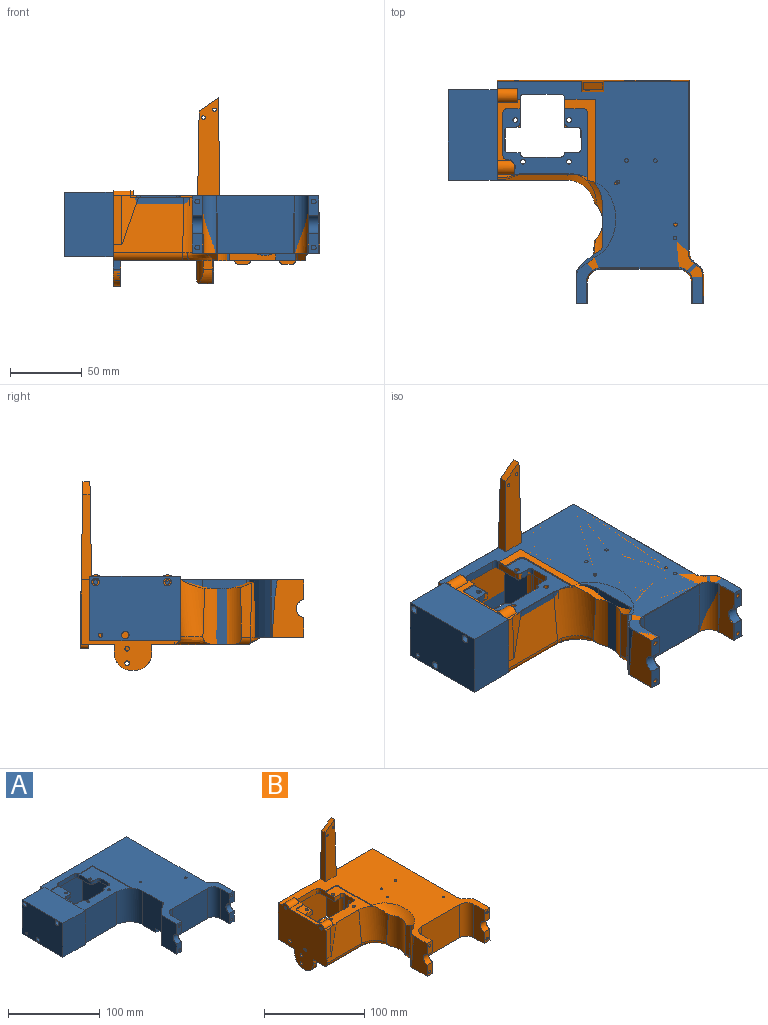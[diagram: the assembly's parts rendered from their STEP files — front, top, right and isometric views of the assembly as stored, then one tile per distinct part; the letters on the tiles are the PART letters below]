
ASSEMBLY  parts=2 mates=1
PART A: 103 faces, bbox 177.1x155.1x65.5 mm
  f0: plane 5.5x4.25mm, normal (-1,0,0), area 19.6mm2, adj f30,f55,f56,f98
  f1: plane 64.7x63mm, normal (-1,0,0), area 807.4mm2, adj f3,f24,f30,f31,f51,f84,f85,f86
  f2: plane 5.5x3.25mm, normal (-1,0,0), area 14.6mm2, adj f56,f96
  f3: plane 133.09x105mm, normal (0,0,-1), area 1435.4mm2, adj f1,f26,f33,f48,f51,f59,f61,f62
  f4: plane 17x6mm, normal (1,0,0), area 85.5mm2, adj f23,f29,f30,f55,f56,f64
  f5: plane 5x5mm, normal (0,-1,0), area 25mm2, adj f22,f23,f56,f64
  f6: plane 8x5mm, normal (0,1,0), area 40mm2, adj f20,f21,f56,f64
  f7: plane 25x5mm, normal (0,1,0), area 125mm2, adj f19,f20,f56,f64
  f8: plane 8.5x5mm, normal (0,1,0), area 42.5mm2, adj f18,f19,f56,f64
  f9: plane 12x5mm, normal (-1,0,0), area 60mm2, adj f17,f18,f56,f64
  f10: plane 5.5x5mm, normal (0,-1,0), area 27.5mm2, adj f16,f17,f56,f64
  f11: plane 17x6mm, normal (-1,0,0), area 85.5mm2, adj f16,f28,f30,f56,f57,f64
  f12: cylinder r=1.65mm len=5mm, axis (0,0,1), area 51.8mm2, adj f56,f64
  f13: cylinder r=1.65mm len=5mm, axis (0,0,1), area 51.8mm2, adj f56,f64
  f14: cylinder r=1.65mm len=5mm, axis (0,0,1), area 51.8mm2, adj f56,f64
  f15: cylinder r=1.65mm len=5mm, axis (0,0,1), area 51.8mm2, adj f56,f64
  f16: cylinder r=3mm len=5mm, axis (0,0,1), area 23.6mm2, adj f10,f11,f56,f64
  f17: cylinder r=3mm len=5mm, axis (0,0,-1), area 23.6mm2, adj f9,f10,f56,f64
  f18: cylinder r=3mm len=5mm, axis (0,0,-1), area 23.6mm2, adj f8,f9,f56,f64
  f19: cylinder r=3mm len=5mm, axis (0,0,1), area 23.6mm2, adj f7,f8,f56,f64
  f20: cylinder r=3mm len=5mm, axis (0,0,-1), area 23.6mm2, adj f6,f7,f56,f64
  f21: cylinder r=3mm len=5mm, axis (0,0,-1), area 23.6mm2, adj f6,f33,f56,f64
  f22: cylinder r=3mm len=5mm, axis (0,0,-1), area 23.6mm2, adj f5,f33,f56,f64
  f23: cylinder r=3mm len=5mm, axis (0,0,1), area 23.6mm2, adj f4,f5,f56,f64
  f24: plane 81.09x62mm, normal (0,0,-1), area 916.9mm2, adj f1,f31,f32,f33,f49,f52,f59,f60
  f25: plane 88x50.06mm, normal (0,0,-1), area 1735.8mm2, adj f26,f34,f35,f36,f37,f39,f40,f41
  f26: plane 5x5mm, normal (0,-1,0), area 25mm2, adj f3,f25,f48,f67
  f27: plane 25x6mm, normal (0,-1,0), area 150mm2, adj f28,f29,f30,f64
  f28: cylinder r=3mm len=6mm, axis (0,0,-1), area 28.3mm2, adj f11,f27,f30,f64
  f29: cylinder r=3mm len=6mm, axis (0,0,1), area 28.3mm2, adj f4,f27,f30,f64
  f30: plane 155.06x143.09mm, normal (0,0,1), area 9490.1mm2, adj f0,f1,f4,f11,f27,f28,f29,f32
  f31: plane 53.09x44mm, normal (0,-1,0), area 2336mm2, adj f1,f24,f32,f56,f91
  f32: cylinder r=20mm len=45mm, axis (0,0,-1), area 1396.1mm2, adj f24,f30,f31,f49,f56,f58
  f33: plane 62x54.7mm, normal (1,0,0), area 2583.9mm2, adj f3,f21,f22,f24,f56,f64,f65,f66
  f34: cylinder r=56.5mm len=40mm, axis (0,0,-1), area 923.4mm2, adj f25,f30,f35,f50
  f35: cylinder r=10mm len=40mm, axis (0,0,-1), area 19.2mm2, adj f25,f30,f34,f36
  f36: plane 40x22.69mm, normal (-1,0,0), area 856.9mm2, adj f25,f30,f35,f37,f38,f54
  f37: plane 13.73x7mm, normal (0,-1,0), area 87.6mm2, adj f25,f36,f39,f54,f82
  f38: plane 13.73x7mm, normal (0,-1,0), area 87.6mm2, adj f30,f36,f39,f54,f80
  f39: plane 40x14.3mm, normal (1,0,0), area 521.3mm2, adj f25,f30,f37,f38,f40,f54
  f40: cylinder r=10mm len=40mm, axis (0,0,-1), area 628.3mm2, adj f25,f30,f39,f41
  f41: plane 54x40mm, normal (0,-1,0), area 2160mm2, adj f25,f30,f40,f42
  f42: cylinder r=10mm len=40mm, axis (0,0,-1), area 628.3mm2, adj f25,f30,f41,f43
  f43: plane 40x14.3mm, normal (-1,0,0), area 521.3mm2, adj f25,f30,f42,f44,f45,f53
  f44: plane 13.73x7mm, normal (0,-1,0), area 87.6mm2, adj f30,f43,f46,f53,f78
  f45: plane 13.73x7mm, normal (0,-1,0), area 87.6mm2, adj f25,f43,f46,f53,f76
  f46: plane 40x23.16mm, normal (1,0,0), area 875.5mm2, adj f25,f30,f44,f45,f47,f53
  f47: cylinder r=56.5mm len=40mm, axis (0,0,-1), area 558.2mm2, adj f25,f30,f46,f48
  f48: plane 122.23x45mm, normal (1,0,0), area 5414.1mm2, adj f3,f25,f26,f30,f47,f51
  f49: plane 45x30.68mm, normal (-1,0,0), area 1328.5mm2, adj f24,f25,f30,f32,f50,f52
  f50: cylinder r=7mm len=40mm, axis (0,0,-1), area 79.5mm2, adj f25,f30,f34,f49
  f51: plane 133.09x45mm, normal (0,1,0), area 5989mm2, adj f1,f3,f30,f48
  f52: plane 8x5mm, normal (0,-1,0), area 40mm2, adj f24,f25,f49,f69
  f53: cylinder r=6.35mm len=12.54mm, axis (-1,0,0), area 125.6mm2, adj f43,f44,f45,f46
  f54: cylinder r=6.35mm len=12.54mm, axis (-1,0,0), area 125.6mm2, adj f36,f37,f38,f39
  f55: plane 16x1mm, normal (0,-1,0), area 16mm2, adj f0,f4,f30,f56,f91
  f56: plane 68.5x59.48mm, normal (0,0,1), area 1924mm2, adj f0,f2,f4,f5,f6,f7,f8,f9
  f57: plane 21.5x1mm, normal (0,-1,0), area 21.5mm2, adj f11,f30,f56,f58
  f58: plane 59.48x1mm, normal (-1,0,0), area 59.5mm2, adj f30,f32,f56,f57
  f59: plane 55x54.7mm, normal (1,0,0), area 2380.5mm2, adj f3,f24,f60,f62,f63,f71,f72,f73
  f60: plane 16x10mm, normal (0,-1,0), area 160mm2, adj f24,f59,f61,f63
  f61: plane 55x54.7mm, normal (-1,0,0), area 2380.5mm2, adj f3,f24,f60,f62,f63,f64,f65,f66
  f62: plane 10x8.72mm, normal (0,1,0), area 87.2mm2, adj f3,f59,f61,f63
  f63: plane 20x10mm, normal (0,0.34,-0.94), area 212.8mm2, adj f59,f60,f61,f62
  f64: plane 55x54.7mm, normal (0,0,-1), area 1216.9mm2, adj f4,f5,f6,f7,f8,f9,f10,f11
  f65: plane 55x39mm, normal (0,-1,0), area 2145mm2, adj f3,f33,f61,f64
  f66: plane 55x39mm, normal (0,1,0), area 2145mm2, adj f24,f33,f61,f64
  f67: plane 107.76x39mm, normal (-1,0,0), area 4164mm2, adj f3,f25,f26,f68,f72,f73
  f68: plane 47x34mm, normal (0,1,0), area 1598mm2, adj f25,f67,f69,f73
  f69: plane 39x29.26mm, normal (1,0,0), area 1102.4mm2, adj f24,f25,f52,f68,f70,f73
  f70: cylinder r=20mm len=39mm, axis (0,0,-1), area 680.2mm2, adj f24,f69,f71,f73
  f71: cylinder r=11.09mm len=39mm, axis (0,0,-1), area 377.2mm2, adj f24,f59,f70,f73
  f72: plane 58.09x39mm, normal (0,-1,0), area 2265.5mm2, adj f3,f59,f67,f73
  f73: plane 107.76x58.09mm, normal (0,0,-1), area 5779mm2, adj f59,f67,f68,f69,f70,f71,f72,f74
  f74: cylinder r=1.25mm len=6mm, axis (0,0,1), area 47.1mm2, adj f30,f73
  f75: cylinder r=1.25mm len=6mm, axis (0,0,1), area 47.1mm2, adj f30,f73
  f76: cylinder r=1.65mm len=15mm, axis (0,-1,0), area 155.5mm2, adj f45,f77
  f77: plane 3.3x3.3mm, normal (0,-1,0), area 8.6mm2, adj f76
  f78: cylinder r=1.65mm len=15mm, axis (0,-1,0), area 155.5mm2, adj f44,f79
  f79: plane 3.3x3.3mm, normal (0,-1,0), area 8.6mm2, adj f78
  f80: cylinder r=1.65mm len=15mm, axis (0,-1,0), area 155.5mm2, adj f38,f81
  f81: plane 3.3x3.3mm, normal (0,-1,0), area 8.6mm2, adj f80
  f82: cylinder r=1.65mm len=15mm, axis (0,-1,0), area 155.5mm2, adj f37,f83
  f83: plane 3.3x3.3mm, normal (0,-1,0), area 8.6mm2, adj f82
  f84: plane 6x5mm, normal (0,1,0), area 30mm2, adj f1,f3,f33,f87
  f85: plane 6x5mm, normal (0,-1,0), area 30mm2, adj f1,f24,f33,f88
  f86: plane 5x2mm, normal (0,0,-1), area 10mm2, adj f1,f33,f87,f88
  f87: cylinder r=12mm len=12mm, axis (-1,0,0), area 94.2mm2, adj f1,f33,f84,f86
  f88: cylinder r=12mm len=12mm, axis (1,0,0), area 94.2mm2, adj f1,f33,f85,f86
  f89: cylinder r=1.57mm len=5mm, axis (-1,0,0), area 49.5mm2, adj f1,f33
  f90: cylinder r=1.57mm len=5mm, axis (-1,0,0), area 49.5mm2, adj f1,f33
  f91: plane 63x45mm, normal (1,0,0), area 379.2mm2, adj f30,f31,f55,f56,f92,f93,f94,f96
  f92: plane 63x34mm, normal (0,0,-1), area 2142mm2, adj f1,f91,f93,f97,f100
  f93: plane 45x34mm, normal (0,-1,0), area 1530mm2, adj f91,f92,f94,f100
  f94: plane 63x34mm, normal (0,0,1), area 2142mm2, adj f91,f93,f97,f100
  f95: cylinder r=1.51mm len=34mm, axis (1,0,0), area 321.7mm2, adj f100,f101
  f96: cylinder r=2.75mm len=34mm, axis (1,0,0), area 587.5mm2, adj f2,f91,f100
  f97: plane 45x34mm, normal (0,1,0), area 1530mm2, adj f1,f91,f92,f94,f100
  f98: cylinder r=2.75mm len=34mm, axis (1,0,0), area 587.5mm2, adj f0,f91,f100
  f99: cylinder r=2.56mm len=34mm, axis (1,0,0), area 547.5mm2, adj f100,f102
  f100: plane 63x45mm, normal (-1,0,0), area 2759.7mm2, adj f92,f93,f94,f95,f96,f97,f98,f99
  f101: plane 3.01x3.01mm, normal (-1,0,0), area 7.1mm2, adj f95
  f102: plane 5.13x5.13mm, normal (-1,0,0), area 20.6mm2, adj f99
PART B: 191 faces, bbox 145.1x157.3x132.7 mm
  f0: cylinder r=1.57mm len=5.29mm, axis (-1,0,0), area 52.1mm2, adj f37,f92
  f1: cylinder r=1.57mm len=5.12mm, axis (-1,0,0), area 50.4mm2, adj f37,f92
  f2: cylinder r=1.25mm len=6mm, axis (0,0,1), area 47.1mm2, adj f38,f60
  f3: cylinder r=1.25mm len=6.62mm, axis (0,0,1), area 48.9mm2, adj f38,f39,f60,f124,f132
  f4: cylinder r=1.65mm len=5mm, axis (0,0,1), area 51.8mm2, adj f96,f180
  f5: cylinder r=1.65mm len=5mm, axis (0,0,1), area 51.8mm2, adj f59,f180
  f6: cylinder r=1.65mm len=5mm, axis (0,0,1), area 51.8mm2, adj f96,f180
  f7: cylinder r=1.65mm len=5mm, axis (0,0,1), area 51.8mm2, adj f59,f180
  f8: cone r=2.1mm half-angle=59deg, axis (0,0.34,-0.94), area 16.2mm2, adj f9
  f9: cylinder r=2.1mm len=27.18mm, axis (0,0.34,-0.94), area 361.5mm2, adj f8,f171
  f10: cone r=1.25mm half-angle=59deg, axis (0,0,-1), area 5.7mm2, adj f11
  f11: cylinder r=1.25mm len=16.5mm, axis (0,0,-1), area 129.6mm2, adj f10,f70
  f12: cylinder r=1.65mm len=5.92mm, axis (0,1,0), area 60.5mm2, adj f80,f89
  f13: cone r=1.65mm half-angle=59deg, axis (0,-1,0), area 10mm2, adj f14
  f14: cylinder r=1.65mm len=15.5mm, axis (0,-1,0), area 160.7mm2, adj f13,f73
  f15: cone r=1.65mm half-angle=59deg, axis (0,-1,0), area 10mm2, adj f16
  f16: cylinder r=1.65mm len=15.5mm, axis (0,-1,0), area 160.7mm2, adj f15,f71
  f17: cone r=1.65mm half-angle=59deg, axis (0,-1,0), area 10mm2, adj f18
  f18: cylinder r=1.65mm len=15.5mm, axis (0,-1,0), area 160.7mm2, adj f17,f77
  f19: cone r=1.65mm half-angle=59deg, axis (0,-1,0), area 10mm2, adj f20
  f20: cylinder r=1.65mm len=15.5mm, axis (0,-1,0), area 160.7mm2, adj f19,f72
  f21: cylinder r=2mm len=8.47mm, axis (-1,0,0), area 106mm2, adj f37,f90
  f22: cylinder r=1.65mm len=5.46mm, axis (-1,0,0), area 56.3mm2, adj f37,f92
  f23: cone r=1.65mm half-angle=59deg, axis (-1,0,0), area 10mm2, adj f29
  f24: cone r=1.65mm half-angle=59deg, axis (-1,0,0), area 6.9mm2, adj f30,f180
  f25: bspline ~5.62x5.27mm, area 31.9mm2, adj f66,f112,f129,f130
  f26: cylinder r=20mm len=55.11mm, axis (0,0,-1), area 1352.3mm2, adj f54,f55,f59,f66,f68,f88,f96,f106
  f27: cylinder r=1.25mm len=5.21mm, axis (0,-1,0), area 40.6mm2, adj f80,f109
  f28: cylinder r=1.25mm len=5.4mm, axis (0,-1,0), area 42.1mm2, adj f80,f109
  f29: cylinder r=1.65mm len=12.1mm, axis (-1,0,0), area 125.4mm2, adj f23,f37
  f30: cylinder r=1.65mm len=12.1mm, axis (-1,0,0), area 125.4mm2, adj f24,f37,f180,f188
  f31: cylinder r=5mm len=14mm, axis (-1,0,0), area 176.9mm2, adj f37,f38,f101
  f32: cylinder r=1.25mm len=5.8mm, axis (0,0,-1), area 45.6mm2, adj f38,f160
  f33: cylinder r=1.25mm len=5.8mm, axis (0,0,-1), area 45.6mm2, adj f38,f160
  f34: cylinder r=1.5mm len=4.19mm, axis (0,1,0), area 39.5mm2, adj f80,f165
  f35: cylinder r=15mm len=30mm, axis (0,1,0), area 527mm2, adj f80,f139,f140,f142,f144,f163,f164,f170
  f36: cylinder r=5mm len=12.08mm, axis (-1,0,0), area 148.1mm2, adj f37,f38,f40,f188,f190
  f37: plane 69.66x66.5mm, normal (-1,0,0), area 3467.5mm2, adj f0,f1,f21,f22,f29,f30,f31,f36
  f38: plane 155.33x143.42mm, normal (0,0,1), area 9483.3mm2, adj f2,f3,f31,f32,f33,f36,f37,f42
  f39: bspline ~16.48x13.99mm, area 114.9mm2, adj f3,f60,f85,f86,f124,f131
  f40: plane 12.08x2.23mm, normal (0,0,1), area 22.3mm2, adj f36,f37,f41,f67,f188
  f41: plane 34.14x11.65mm, normal (0.24,-0.97,0.03), area 205.4mm2, adj f40,f43,f67,f180,f188
  f42: plane 2.08x1mm, normal (0,1,0), area 2.1mm2, adj f38,f180,f184,f190
  f43: plane 49.22x38.39mm, normal (0,-0.99,0.12), area 1490.2mm2, adj f37,f41,f67,f112,f130,f180
  f44: plane 8x5mm, normal (0,-1,0), area 40mm2, adj f53,f96,f145,f180
  f45: plane 8.5x5mm, normal (0,-1,0), area 42.5mm2, adj f54,f96,f149,f180
  f46: cylinder r=3mm len=5mm, axis (0,0,1), area 23.6mm2, adj f47,f55,f59,f180
  f47: plane 8.5x5mm, normal (0,1,0), area 42.5mm2, adj f46,f48,f59,f180
  f48: cylinder r=3mm len=5mm, axis (0,0,1), area 23.6mm2, adj f47,f49,f59,f180
  f49: plane 25x5mm, normal (0,1,0), area 125mm2, adj f48,f50,f59,f180
  f50: cylinder r=3mm len=5mm, axis (0,0,1), area 23.6mm2, adj f49,f51,f59,f180
  f51: plane 8x5mm, normal (0,1,0), area 40mm2, adj f50,f52,f59,f180
  f52: cylinder r=3mm len=24mm, axis (0,0,1), area 66.9mm2, adj f51,f56,f59,f92,f150,f180
  f53: cylinder r=3mm len=24mm, axis (0,0,1), area 66.9mm2, adj f44,f56,f92,f96,f150,f180
  f54: cylinder r=3mm len=24mm, axis (0,0,1), area 49.5mm2, adj f26,f45,f55,f96,f151,f180
  f55: plane 24x12mm, normal (-1,0,0), area 158.2mm2, adj f26,f46,f54,f59,f151,f180
  f56: plane 24x12mm, normal (1,0,0), area 288mm2, adj f52,f53,f150,f180
  f57: plane 2.75x0.39mm, normal (-1,0.03,0.02), area 0.5mm2, adj f108,f112,f176
  f58: cylinder r=5mm len=4.59mm, axis (-0.03,-1,0), area 4mm2, adj f66,f129,f172,f176
  f59: plane 56.86x17.83mm, normal (0,0,-1), area 364.6mm2, adj f5,f7,f26,f46,f47,f48,f49,f50
  f60: plane 118.67x56.29mm, normal (0,0,-1), area 4877.7mm2, adj f2,f3,f39,f83,f84,f85,f86,f123
  f61: plane 20x6.19mm, normal (0,0,-1), area 115.9mm2, adj f63,f80,f135,f142,f144,f170
  f62: plane 6.5x2.33mm, normal (0,0,-1), area 15.1mm2, adj f63,f64,f80,f139
  f63: cylinder r=2.5mm len=2.5mm, axis (0,-1,0), area 9.1mm2, adj f61,f62,f80,f139,f144
  f64: cylinder r=2.5mm len=2.5mm, axis (0,1,0), area 9.1mm2, adj f62,f69,f80,f139
  f65: cylinder r=3mm len=39.07mm, axis (0.03,0,-1), area 87mm2, adj f69,f84,f140,f141,f166,f168
  f66: plane 81.04x67.88mm, normal (0,0,-1), area 553.5mm2, adj f25,f26,f37,f58,f68,f82,f85,f87
  f67: plane 34.14x6.15mm, normal (0,-1,0.03), area 207.5mm2, adj f37,f40,f41,f43
  f68: plane 39.55x14.34mm, normal (-1,0,-0.02), area 429.4mm2, adj f26,f59,f66,f95
  f69: plane 117.15x9.81mm, normal (0,0,-1), area 648.1mm2, adj f64,f65,f79,f80,f84,f139,f141,f143
  f70: plane 84.66x23.86mm, normal (0,0,-1), area 736.7mm2, adj f11,f37,f80,f85,f88,f89,f90,f91
  f71: plane 13.73x7.7mm, normal (0,-1,0), area 95.5mm2, adj f16,f74,f97,f133,f136
  f72: plane 13.73x8.4mm, normal (0,-1,0), area 103.4mm2, adj f20,f76,f78,f98,f133
  f73: plane 13.73x7.24mm, normal (0,-1,0), area 89.2mm2, adj f14,f38,f74,f97,f136
  f74: plane 41.28x16.28mm, normal (1,0,0.02), area 535.5mm2, adj f38,f71,f73,f97,f113,f133
  f75: plane 54x40mm, normal (0,-1,0.02), area 2132.5mm2, adj f38,f113,f114,f133
  f76: plane 41.28x16.28mm, normal (-1,0,0.02), area 535.5mm2, adj f38,f72,f77,f98,f114,f133
  f77: plane 13.73x7.48mm, normal (0,-1,0), area 90.8mm2, adj f18,f38,f76,f78,f98
  f78: plane 41.28x20.44mm, normal (1,0,0.02), area 708.5mm2, adj f38,f72,f77,f98,f117,f133
  f79: plane 119.58x45mm, normal (1,0,0.02), area 5353.8mm2, adj f38,f69,f80,f115,f186
  f80: plane 134.34x116.35mm, normal (0,1,0.02), area 6244.3mm2, adj f12,f27,f28,f34,f35,f37,f38,f61
  f81: plane 37.69x7.52mm, normal (-1,0.03,0.02), area 248.5mm2, adj f108,f116,f128,f176
  f82: plane 27.84x10.28mm, normal (1,-0.03,-0.03), area 225.2mm2, adj f66,f83,f123,f133,f173,f187
  f83: plane 56.06x34.36mm, normal (0,1,-0.03), area 1825.1mm2, adj f60,f82,f84,f123,f133
  f84: plane 116.19x39mm, normal (-1,0,-0.03), area 4491.3mm2, adj f60,f65,f69,f83,f133,f186
  f85: plane 55.55x55.21mm, normal (1,0,-0.03), area 2462.1mm2, adj f39,f60,f66,f70,f86,f106,f107,f119
  f86: plane 10.46x5.57mm, normal (0,1,-0.03), area 18.2mm2, adj f39,f60,f85
  f87: plane 27.85x11.54mm, normal (1,0,-0.03), area 276.7mm2, adj f66,f124,f131,f173
  f88: plane 39x18.36mm, normal (-1,0,0), area 689.6mm2, adj f26,f70,f89,f96
  f89: plane 55.01x39.47mm, normal (0,-1,-0.03), area 2106.6mm2, adj f12,f70,f88,f90,f96
  f90: plane 39.57x17.93mm, normal (1,0,-0.02), area 611.5mm2, adj f21,f70,f89,f91,f96
  f91: plane 39x3.68mm, normal (0,-1,-0.03), area 117.1mm2, adj f70,f90,f92,f96
  f92: plane 57.8x37.53mm, normal (1,0,-0.02), area 1454.7mm2, adj f0,f1,f22,f52,f53,f59,f66,f70
  f93: plane 39x3.68mm, normal (0,1,-0.03), area 117.1mm2, adj f59,f66,f92,f94
  f94: plane 39x6.79mm, normal (1,0,-0.02), area 144.8mm2, adj f59,f66,f93,f95
  f95: plane 55.22x39mm, normal (0,0.99,-0.12), area 2143.1mm2, adj f59,f66,f68,f94
  f96: plane 56.86x27.68mm, normal (0,0,-1), area 682.1mm2, adj f4,f6,f26,f44,f45,f53,f54,f88
  f97: cylinder r=6.35mm len=12.54mm, axis (-1,0,0), area 131.8mm2, adj f71,f73,f74,f136
  f98: cylinder r=6.35mm len=12.54mm, axis (-1,0,0), area 138.1mm2, adj f72,f76,f77,f78
  f99: plane 39.91x3.1mm, normal (-0.47,0.88,0.02), area 109.4mm2, adj f38,f116,f118,f126
  f100: plane 40x2.17mm, normal (0.57,0.82,0.02), area 71.8mm2, adj f38,f115,f117,f133
  f101: plane 9.62x3.59mm, normal (1,0,0.02), area 24.5mm2, adj f31,f38
  f102: plane 6.23x6mm, normal (0,0,-1), area 37.4mm2, adj f80,f134,f135,f170
  f103: plane 6x5.32mm, normal (0,-1,0), area 31.6mm2, adj f37,f66,f92,f122
  f104: plane 6x5.32mm, normal (0,1,0), area 31.6mm2, adj f37,f70,f92,f121
  f105: plane 5.01x2mm, normal (0,0,-1), area 10mm2, adj f37,f92,f121,f122
  f106: plane 6.64x6mm, normal (0,-1,0), area 39.2mm2, adj f26,f66,f85,f120
  f107: plane 6.64x6mm, normal (0,1,0), area 39.2mm2, adj f26,f70,f85,f119
  f108: revolved ~53.85x21.51mm, area 557.1mm2, adj f38,f57,f81,f112,f116,f174,f175,f176
  f109: plane 68.73x15.87mm, normal (0,-1,0.02), area 908.4mm2, adj f27,f28,f38,f110,f111,f189
  f110: plane 68.38x7.26mm, normal (1,0,0.02), area 414.7mm2, adj f38,f80,f109,f189
  f111: plane 59.07x7.26mm, normal (-1,0,0.02), area 367.8mm2, adj f38,f80,f109,f189
  f112: cylinder r=20mm len=43.04mm, axis (0.02,0.12,0.99), area 1129.6mm2, adj f25,f38,f43,f57,f108,f129,f176,f177
  f113: cylinder r=10mm len=40.07mm, axis (-0.02,0.02,1), area 628.4mm2, adj f38,f74,f75,f133
  f114: cylinder r=10mm len=40.07mm, axis (0.02,0.02,1), area 628.4mm2, adj f38,f75,f76,f133
  f115: cylinder r=10mm len=43.84mm, axis (0.02,0.01,-1), area 397.6mm2, adj f38,f79,f100,f133,f186
  f116: cylinder r=10mm len=39.97mm, axis (-0.02,0.01,-1), area 410.4mm2, adj f38,f81,f99,f108,f127
  f117: cylinder r=10mm len=40.02mm, axis (-0.02,-0.01,1), area 384mm2, adj f38,f78,f100,f133
  f118: cylinder r=10mm len=39.95mm, axis (0.02,-0.01,1), area 330.4mm2, adj f38,f99,f125,f136,f137
  f119: cylinder r=12mm len=6.7mm, axis (1,0,0), area 18.3mm2, adj f26,f85,f107,f171
  f120: cylinder r=12mm len=10.11mm, axis (-1,0,0), area 95.3mm2, adj f26,f85,f106,f171
  f121: cylinder r=12mm len=12mm, axis (1,0,0), area 96.3mm2, adj f37,f92,f104,f105
  f122: cylinder r=12mm len=12mm, axis (-1,0,0), area 96.3mm2, adj f37,f92,f103,f105
  f123: cylinder r=12mm len=31.04mm, axis (0.03,1,0), area 335.7mm2, adj f60,f82,f83,f124,f173
  f124: cylinder r=12mm len=24.33mm, axis (0,1,0), area 329.7mm2, adj f3,f39,f60,f87,f123,f132,f173
  f125: bspline ~5.29x4.62mm, area 0.7mm2, adj f118,f126,f133,f137
  f126: cylinder r=5mm len=2.42mm, axis (0.88,0.47,0), area 0.2mm2, adj f99,f125,f127,f133
  f127: bspline ~10.22x7.26mm, area 16.9mm2, adj f116,f126,f128,f133,f187
  f128: cylinder r=5mm len=15.5mm, axis (-0.03,-1,0), area 67.3mm2, adj f66,f81,f127,f176,f187
  f129: bspline ~25.63x21.48mm, area 236.6mm2, adj f25,f58,f66,f112,f176
  f130: cylinder r=5mm len=48.38mm, axis (1,0,0), area 409.6mm2, adj f25,f37,f43,f66
  f131: plane 27.42x7.88mm, normal (0.86,0.5,-0.05), area 219.1mm2, adj f39,f66,f85,f87
  f132: cylinder r=14.06mm len=1.42mm, axis (-0.04,0.88,0.48), area 0.1mm2, adj f3,f60,f124
  f133: plane 89.08x30.33mm, normal (0,0,-1), area 874.4mm2, adj f71,f72,f74,f75,f76,f78,f82,f83
  f134: cylinder r=2.5mm len=6.23mm, axis (0,1,0), area 24.4mm2, adj f70,f80,f102,f170
  f135: cylinder r=2.5mm len=6.23mm, axis (0,-1,0), area 24.4mm2, adj f61,f80,f102,f170
  f136: plane 40x22mm, normal (-1,0,0), area 777.2mm2, adj f38,f71,f73,f97,f118,f133,f137
  f137: plane 2.09x0.04mm, normal (0,-1,0), area 0mm2, adj f118,f125,f133,f136
  f138: cylinder r=3mm len=39.09mm, axis (-0.03,0,-1), area 90.4mm2, adj f70,f85,f167,f169
  f139: plane 12x11mm, normal (0,-1,0), area 100.2mm2, adj f35,f62,f63,f64,f69,f140,f143,f144
  f140: plane 9.5x5.24mm, normal (0,0,-1), area 36.6mm2, adj f35,f65,f139,f141,f143,f168,f170
  f141: plane 9.75x2.49mm, normal (-1,0,0), area 20mm2, adj f65,f69,f140,f143
  f142: plane 5.51x0.9mm, normal (1,0,0), area 5mm2, adj f35,f61,f144,f170
  f143: cylinder r=3mm len=9.5mm, axis (0,0,-1), area 44.8mm2, adj f69,f139,f140,f141
  f144: cylinder r=3mm len=9.29mm, axis (0,0,1), area 31.7mm2, adj f35,f61,f63,f139,f142
  f145: plane 20x6mm, normal (1,0,0), area 107.2mm2, adj f38,f44,f96,f146,f178,f180
  f146: cylinder r=3mm len=6mm, axis (0,0,1), area 28.3mm2, adj f38,f96,f145,f147
  f147: plane 25x6mm, normal (0,-1,0), area 150mm2, adj f38,f96,f146,f148
  f148: cylinder r=3mm len=6mm, axis (0,0,1), area 28.3mm2, adj f38,f96,f147,f149
  f149: plane 20x6mm, normal (-1,0,0), area 107.2mm2, adj f38,f45,f96,f148,f179,f180
  f150: plane 15.78x0.67mm, normal (0,0,1), area 9.7mm2, adj f52,f53,f56,f92
  f151: plane 6.49x0.44mm, normal (0,0,1), area 2mm2, adj f26,f54,f55
  f152: cylinder r=3mm len=3mm, axis (0,0,-1), area 0.9mm2, adj f60,f153,f159,f160
  f153: plane 39x0.2mm, normal (0,-1,0), area 7.8mm2, adj f60,f152,f154,f160
  f154: cylinder r=3mm len=3mm, axis (0,0,-1), area 0.9mm2, adj f60,f153,f155,f160
  f155: plane 14x0.2mm, normal (1,0,0), area 2.8mm2, adj f60,f154,f156,f160
  f156: cylinder r=3mm len=3mm, axis (0,0,-1), area 0.9mm2, adj f60,f155,f157,f160
  f157: plane 39x0.2mm, normal (0,1,0), area 7.8mm2, adj f60,f156,f158,f160
  f158: cylinder r=3mm len=3mm, axis (0,0,-1), area 0.9mm2, adj f60,f157,f159,f160
  f159: plane 14x0.2mm, normal (-1,0,0), area 2.8mm2, adj f60,f152,f158,f160
  f160: plane 45x20mm, normal (0,0,-1), area 882.5mm2, adj f32,f33,f152,f153,f154,f155,f156,f157
  f161: cylinder r=10mm len=10mm, axis (0,0,1), area 53.6mm2, adj f162,f164,f165,f170
  f162: plane 16.21x1.4mm, normal (0,0,-1), area 18.1mm2, adj f161,f163,f165,f170
  f163: cylinder r=10mm len=10mm, axis (0,0,1), area 42.5mm2, adj f35,f162,f164,f165,f170
  f164: plane 11.69x1.4mm, normal (0,0,1), area 14.1mm2, adj f35,f161,f163,f165,f170
  f165: plane 10x6mm, normal (0,-1,0), area 52.9mm2, adj f34,f161,f162,f163,f164
  f166: plane 2.6x1.47mm, normal (-1,0,0), area 0.3mm2, adj f60,f65,f168
  f167: plane 2.6x1.47mm, normal (1,0,0), area 0.3mm2, adj f60,f138,f169
  f168: cylinder r=3mm len=29.5mm, axis (0,0,-1), area 103.9mm2, adj f60,f65,f140,f166,f170
  f169: cylinder r=3mm len=39mm, axis (0,0,-1), area 133.2mm2, adj f60,f70,f138,f167,f170
  f170: plane 50.23x41.5mm, normal (0,-1,0), area 1030.8mm2, adj f35,f60,f61,f70,f102,f134,f135,f140
  f171: plane 20.44x11.43mm, normal (0,0.34,-0.94), area 198.9mm2, adj f9,f26,f85,f119,f120
  f172: plane 0.95x0.02mm, normal (-1,0.02,0), area 0mm2, adj f58,f66
  f173: cylinder r=25.5mm len=37.24mm, axis (0,0,-1), area 1234.3mm2, adj f66,f82,f87,f123,f124
  f174: plane 1.97x0.22mm, normal (0,0,1), area 0.1mm2, adj f108,f175,f176
  f175: plane 0.79x0.04mm, normal (-1,0.02,0), area 0mm2, adj f108,f174,f176
  f176: cylinder r=18.5mm len=39.71mm, axis (0,0,-1), area 1109.9mm2, adj f57,f58,f66,f81,f108,f112,f128,f129
  f177: plane 1x0.5mm, normal (0,1,0), area 0.4mm2, adj f38,f112,f180,f183
  f178: plane 9x1mm, normal (0,-1,0), area 9mm2, adj f38,f145,f180,f181
  f179: plane 13x1mm, normal (0,-1,0), area 13mm2, adj f38,f149,f180,f182
  f180: plane 59.32x50.32mm, normal (0,0,1), area 1123.6mm2, adj f4,f5,f6,f7,f24,f30,f41,f42
  f181: cylinder r=3mm len=3mm, axis (0,0,1), area 4.7mm2, adj f38,f178,f180,f185
  f182: cylinder r=3mm len=3mm, axis (0,0,1), area 4.7mm2, adj f38,f179,f180,f183
  f183: plane 47x1mm, normal (-1,0,0), area 47mm2, adj f38,f177,f180,f182
  f184: cylinder r=3mm len=3mm, axis (0,0,1), area 4.7mm2, adj f38,f42,f180,f185
  f185: plane 29.5x1mm, normal (1,0,0), area 29.5mm2, adj f38,f180,f181,f184
  f186: plane 8.95x8.26mm, normal (0,-0.5,-0.87), area 60.6mm2, adj f69,f79,f84,f115,f133
  f187: plane 9.5x9.45mm, normal (0,-0.5,-0.87), area 50.8mm2, adj f66,f82,f127,f128,f133
  f188: plane 7.8x4.5mm, normal (1,0,0), area 25mm2, adj f30,f36,f40,f41,f180,f190
  f189: plane 13.29x9.31mm, normal (-0.57,0,0.82), area 81.6mm2, adj f80,f109,f110,f111
  f190: plane 4.54x3.59mm, normal (0.71,0.71,0), area 10.8mm2, adj f36,f38,f42,f180,f188
PLACE A t=(-0.94,-27.16,-28.59)mm
PLACE B t=(-15.4,2.03,-6.09)mm fixed
MATE parallel A.f30 <-> B.f38  axis (0,0,-1) through (-32.9,-74.54,16.41)mm
